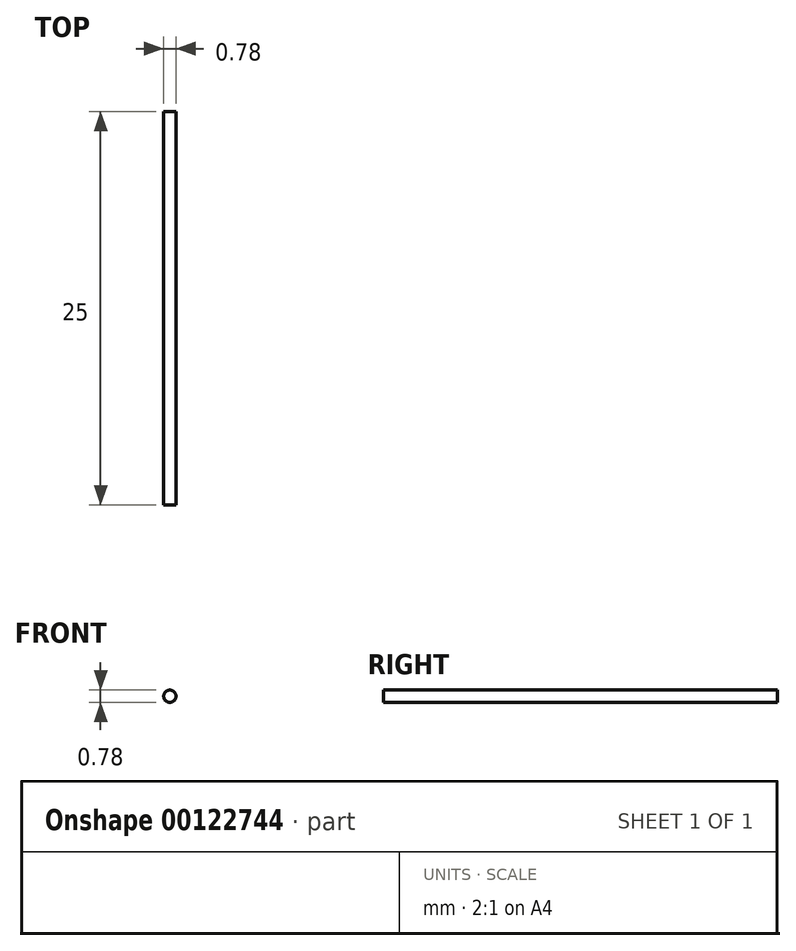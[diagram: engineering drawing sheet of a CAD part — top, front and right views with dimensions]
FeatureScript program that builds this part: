
annotation { "Feature Type Name" : "Feature", "Feature Type Description" : "" }
export const myFeature = defineFeature(function(context is Context, id is Id, definition is map)
    precondition{}
    {
        {
            var Q0;
            Q0=qCreatedBy(makeId("Front.planeOp"),FACE);
            var sketch = newSketch(context, id + "F0", { "sketchPlane" : qUnion([Q0])});
            skCircle(sketch, "E0", {"center": v(0, 0) * mm, "radius": 0.4 * mm});
            skSolve(sketch);
        }
        {
            var Q0;
            Q0 = qSketchRegion(id + "F0", true);
            extrude(context, id + "F1", {"entities" : qUnion([Q0]), "depth" : 25 * mm});
        }
    });
